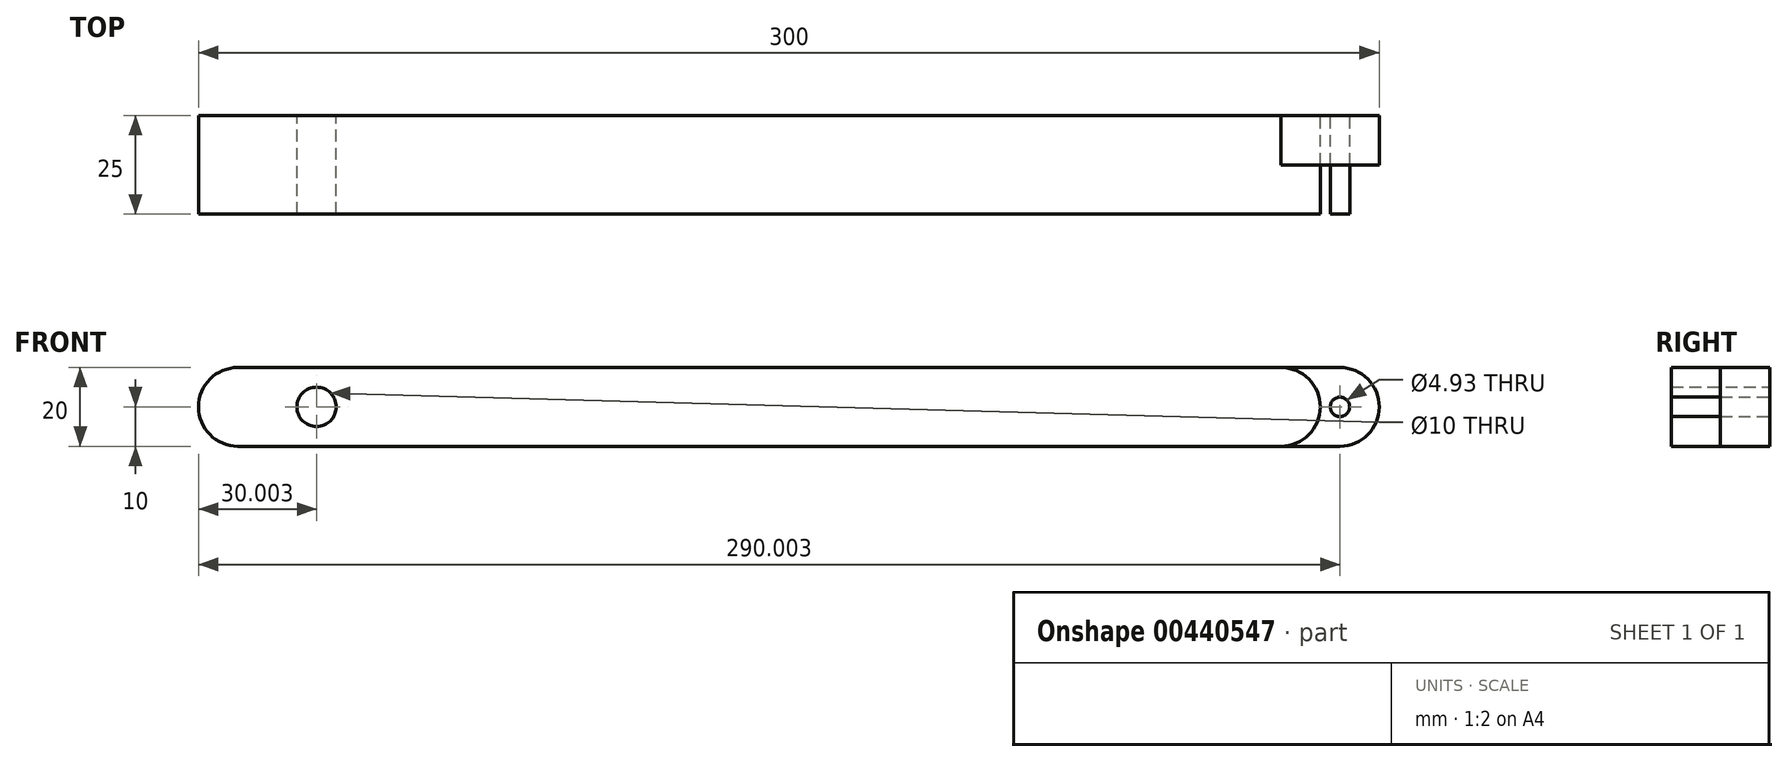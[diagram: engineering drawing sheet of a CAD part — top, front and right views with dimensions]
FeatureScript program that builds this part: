
annotation { "Feature Type Name" : "Feature", "Feature Type Description" : "" }
export const myFeature = defineFeature(function(context is Context, id is Id, definition is map)
    precondition{}
    {
        {
            var Q0;
            Q0=qCreatedBy(makeId("Front.planeOp"),FACE);
            var sketch = newSketch(context, id + "F0", { "sketchPlane" : qUnion([Q0])});
            skLineSegment(sketch, "E0.bottom", {"start": v(-166.67, 10) * mm, "end": v(98.33, 10) * mm});
            skLineSegment(sketch, "E0.top", {"start": v(-166.67, -10) * mm, "end": v(98.33, -10) * mm});
            skLineSegment(sketch, "E0.left", {"start": v(-176.67, 0) * mm, "end": v(-176.67, 0) * mm});
            skLineSegment(sketch, "E0.right", {"start": v(123.33, 0) * mm, "end": v(123.33, 0) * mm});
            skPoint(sketch, "E0.middle", {"position": v(1.8, 0) * mm});
            skCircle(sketch, "E1", {"center": v(113.33, 0) * mm, "radius": 2.46 * mm});
            skArc(sketch, "E2.filletArc", {"start": v(123.33, 0) * mm, "mid": v(120.4, 7.07) * mm, "end": v(113.33, 10) * mm});
            skArc(sketch, "E3.filletArc", {"start": v(113.33, -10) * mm, "mid": v(120.4, -7.07) * mm, "end": v(123.33, 0) * mm});
            skLineSegment(sketch, "E4", {"start": v(108.33, 0) * mm, "end": v(108.33, 0) * mm});
            skPoint(sketch, "E5.newPointB", {"position": v(108.33, 10) * mm});
            skArc(sketch, "E5.filletArc", {"start": v(108.33, 0) * mm, "mid": v(105.4, 7.07) * mm, "end": v(98.33, 10) * mm});
            skArc(sketch, "E6.filletArc", {"start": v(98.33, -10) * mm, "mid": v(105.4, -7.07) * mm, "end": v(108.33, 0) * mm});
            skLineSegment(sketch, "E7", {"start": v(98.33, -10) * mm, "end": v(113.33, -10) * mm});
            skLineSegment(sketch, "E8", {"start": v(113.33, 10) * mm, "end": v(98.33, 10) * mm});
            skLineSegment(sketch, "E9", {"start": v(-146.67, 10) * mm, "end": v(-146.67, -10) * mm});
            skLineSegment(sketch, "E10", {"start": v(-176.67, 0) * mm, "end": v(-146.67, 0) * mm});
            skArc(sketch, "E11.filletArc", {"start": v(-166.67, 10) * mm, "mid": v(-173.74, 7.07) * mm, "end": v(-176.67, 0) * mm});
            skArc(sketch, "E12.filletArc", {"start": v(-176.67, 0) * mm, "mid": v(-173.74, -7.07) * mm, "end": v(-166.67, -10) * mm});
            skLineSegment(sketch, "E13", {"start": v(-26.67, 10) * mm, "end": v(-26.67, -10) * mm});
            skLineSegment(sketch, "E14", {"start": v(-146.67, 0) * mm, "end": v(-26.67, 0) * mm});
            skLineSegment(sketch, "E15", {"start": v(-96.67, 10) * mm, "end": v(-96.67, -10) * mm});
            skPoint(sketch, "E16", {"position": v(-96.67, 0) * mm});
            skSolve(sketch);
        }
        {
            var Q0;
            {var subQ0=sQuery(id+"F0.wireOp",EDGE,"E5.filletArc");Q0=makeQuery(id+"F0.imprint","IMPRINT",FACE,{"disambiguationData":[TD([[makeQuery(id+"F0.imprint","IMPRINT",EDGE,{"derivedFrom":subQ0}),1.0]])]});}
            var Q1;
            {var subQ4=sQuery(id+"F0.wireOp",EDGE,"E10");Q1=makeQuery(id+"F0.imprint","IMPRINT",FACE,{"disambiguationData":[TD([[makeQuery(id+"F0.imprint","IMPRINT",EDGE,{"derivedFrom":subQ4}),1.0]])]});}
            var Q2;
            {var subQ4=sQuery(id+"F0.wireOp",EDGE,"E10");Q2=makeQuery(id+"F0.imprint","IMPRINT",FACE,{"disambiguationData":[TD([[makeQuery(id+"F0.imprint","IMPRINT",EDGE,{"derivedFrom":subQ4}),-1.0]])]});}
            var Q3;
            Q3=makeQuery(id+"F0.imprint","IMPRINT",FACE,{"disambiguationData":[TD([[makeQuery(id+"F0.imprint","IMPRINT",EDGE,{"derivedFrom":sQuery(id+"F0.wireOp",EDGE,"E1")}),1.0]])]});
            var Q4;
            {var subQ5=sQuery(id+"F0.wireOp",EDGE,"E14");Q4=makeQuery(id+"F0.imprint","IMPRINT",FACE,{"disambiguationData":[TD([[makeQuery(id+"F0.imprint","IMPRINT",EDGE,{"derivedFrom":subQ5}),-1.0]])]});}
            var Q5;
            {var subQ5=sQuery(id+"F0.wireOp",EDGE,"E14");Q5=makeQuery(id+"F0.imprint","IMPRINT",FACE,{"disambiguationData":[TD([[makeQuery(id+"F0.imprint","IMPRINT",EDGE,{"derivedFrom":subQ5}),1.0]])]});}
            extrude(context, id + "F1", {"entities" : qUnion([Q0, Q1, Q2, Q3, Q4, Q5]), "depth" : 25 * mm});
        }
        {
            var Q0;
            Q0=makeQuery(id+"F0.imprint","IMPRINT",FACE,{"disambiguationData":[TD([[makeQuery(id+"F0.imprint","IMPRINT",EDGE,{"derivedFrom":sQuery(id+"F0.wireOp",EDGE,"E1")}),-1.0]])]});
            extrude(context, id + "F2", {"entities" : qUnion([Q0]), "depth" : 12.5 * mm});
        }
        {
            var Q0;
            Q0=sQuery(id+"F0.wireOp",VERTEX,"E10.end");
            var Q1;
            Q1=makeQuery(id+"F1.opExtrude","SWEPT_BODY",BODY,{"disambiguationData":[OSD([sQuery(id+"F0.wireOp",EDGE,"E0.bottom"),sQuery(id+"F0.wireOp",EDGE,"E0.top"),sQuery(id+"F0.wireOp",EDGE,"E5.filletArc"),sQuery(id+"F0.wireOp",EDGE,"E6.filletArc"),sQuery(id+"F0.wireOp",EDGE,"E11.filletArc"),sQuery(id+"F0.wireOp",EDGE,"E12.filletArc")])]});
            hole(context, id + "F3", {"style" : HoleStyle.SIMPLE, "endStyle" : HoleEndStyle.THROUGH, "oppositeDirection" : true, "holeDiameter" : 10 * mm, "isTappedThrough" : true, "tappedDepth" : 12 * mm, "tapClearance" : 3, "startFromSketch" : true, "locations" : qUnion([Q0]), "scope" : qUnion([Q1])});
        }
        {
            var Q0;
            Q0=sQuery(id+"F0.wireOp",VERTEX,"E14.end");
            var Q1;
            Q1=makeQuery(id+"F1.opExtrude","SWEPT_BODY",BODY,{"disambiguationData":[OSD([sQuery(id+"F0.wireOp",EDGE,"E1")])]});
            hole(context, id + "F4", {"style" : HoleStyle.SIMPLE, "endStyle" : HoleEndStyle.THROUGH, "oppositeDirection" : true, "holeDiameter" : 10 * mm, "isTappedThrough" : true, "tappedDepth" : 12 * mm, "tapClearance" : 3, "startFromSketch" : true, "locations" : qUnion([Q0]), "scope" : qUnion([Q1])});
        }
        {
            var Q0;
            Q0=sQuery(id+"F0.wireOp",VERTEX,"E16");
            var Q1;
            Q1=makeQuery(id+"F1.opExtrude","SWEPT_BODY",BODY,{"disambiguationData":[OSD([sQuery(id+"F0.wireOp",EDGE,"E1")])]});
            hole(context, id + "F5", {"style" : HoleStyle.SIMPLE, "endStyle" : HoleEndStyle.THROUGH, "oppositeDirection" : true, "holeDiameter" : 6 * mm, "isTappedThrough" : true, "tappedDepth" : 12 * mm, "tapClearance" : 3, "startFromSketch" : true, "locations" : qUnion([Q0]), "scope" : qUnion([Q1])});
        }
    });
